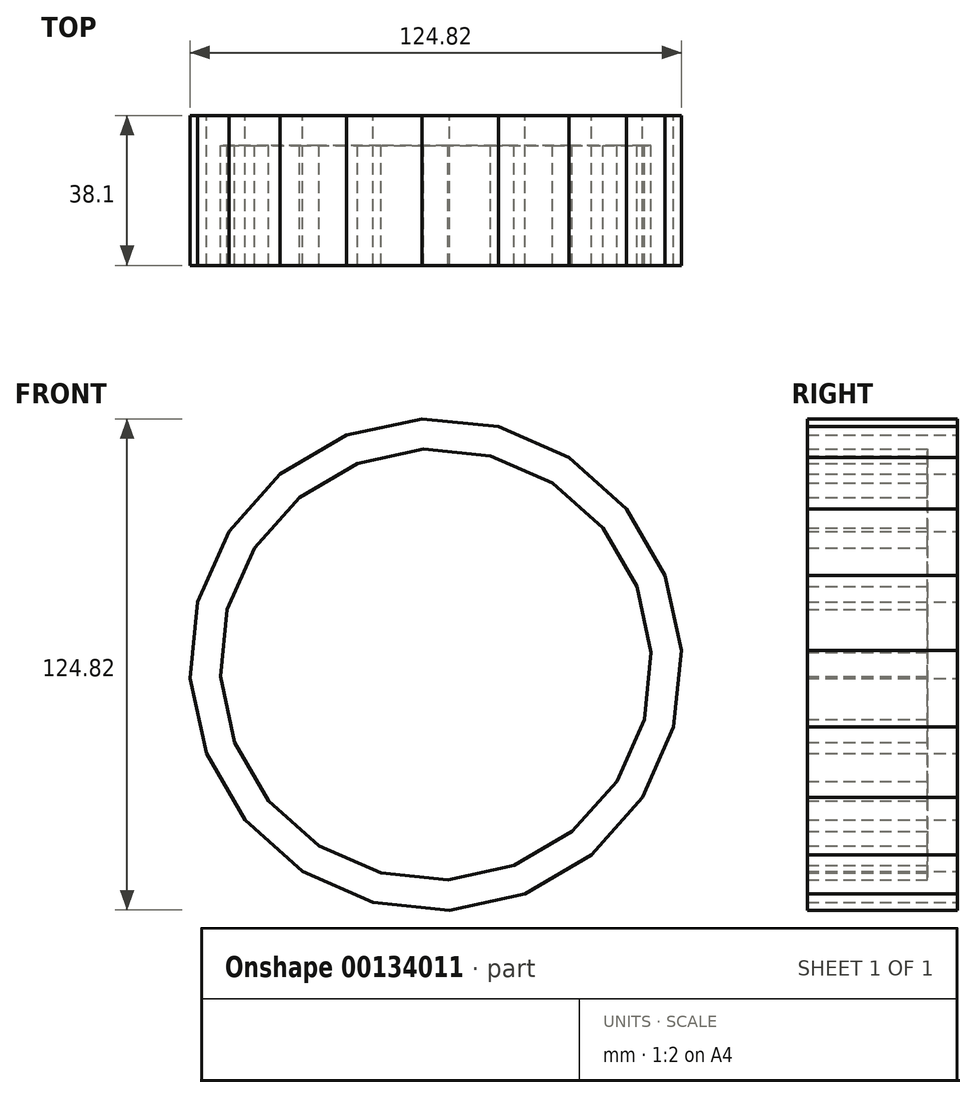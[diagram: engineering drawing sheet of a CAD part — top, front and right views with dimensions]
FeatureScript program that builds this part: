
annotation { "Feature Type Name" : "Feature", "Feature Type Description" : "" }
export const myFeature = defineFeature(function(context is Context, id is Id, definition is map)
    precondition{}
    {
        {
            var Q0;
            Q0=qCreatedBy(makeId("Front.planeOp"),FACE);
            var sketch = newSketch(context, id + "F0", { "sketchPlane" : qUnion([Q0])});
            skCircle(sketch, "E0.cCircle", {"center": v(0, 0) * mm, "radius": 61.74 * mm, "construction": true});
            skLineSegment(sketch, "E0.0", {"start": v(-48.41, -39.55) * mm, "end": v(-58.27, -22.65) * mm});
            skLineSegment(sketch, "E0.1", {"start": v(-58.27, -22.65) * mm, "end": v(-62.41, -3.54) * mm});
            skLineSegment(sketch, "E0.2", {"start": v(-62.41, -3.54) * mm, "end": v(-60.45, 15.92) * mm});
            skLineSegment(sketch, "E0.3", {"start": v(-60.45, 15.92) * mm, "end": v(-52.57, 33.82) * mm});
            skLineSegment(sketch, "E0.4", {"start": v(-52.57, 33.82) * mm, "end": v(-39.55, 48.41) * mm});
            skLineSegment(sketch, "E0.5", {"start": v(-39.55, 48.41) * mm, "end": v(-22.65, 58.27) * mm});
            skLineSegment(sketch, "E0.6", {"start": v(-22.65, 58.27) * mm, "end": v(-3.54, 62.41) * mm});
            skLineSegment(sketch, "E0.7", {"start": v(-3.54, 62.41) * mm, "end": v(15.92, 60.45) * mm});
            skLineSegment(sketch, "E0.8", {"start": v(15.92, 60.45) * mm, "end": v(33.82, 52.57) * mm});
            skLineSegment(sketch, "E0.9", {"start": v(33.82, 52.57) * mm, "end": v(48.41, 39.55) * mm});
            skLineSegment(sketch, "E0.10", {"start": v(48.41, 39.55) * mm, "end": v(58.27, 22.65) * mm});
            skLineSegment(sketch, "E0.11", {"start": v(58.27, 22.65) * mm, "end": v(62.41, 3.54) * mm});
            skLineSegment(sketch, "E0.12", {"start": v(62.41, 3.54) * mm, "end": v(60.45, -15.92) * mm});
            skLineSegment(sketch, "E0.13", {"start": v(60.45, -15.92) * mm, "end": v(52.57, -33.82) * mm});
            skLineSegment(sketch, "E0.14", {"start": v(52.57, -33.82) * mm, "end": v(39.55, -48.41) * mm});
            skLineSegment(sketch, "E0.15", {"start": v(39.55, -48.41) * mm, "end": v(22.65, -58.27) * mm});
            skLineSegment(sketch, "E0.16", {"start": v(22.65, -58.27) * mm, "end": v(3.54, -62.41) * mm});
            skLineSegment(sketch, "E0.17", {"start": v(3.54, -62.41) * mm, "end": v(-15.92, -60.45) * mm});
            skLineSegment(sketch, "E0.18", {"start": v(-15.92, -60.45) * mm, "end": v(-33.82, -52.57) * mm});
            skLineSegment(sketch, "E0.19", {"start": v(-33.82, -52.57) * mm, "end": v(-48.41, -39.55) * mm});
            skPoint(sketch, "E0.0.midPoint", {"position": v(-53.34, -31.1) * mm});
            skSolve(sketch);
        }
        {
            var Q0;
            Q0 = qSketchRegion(id + "F0", true);
            extrude(context, id + "F1", {"entities" : qUnion([Q0]), "endBound" : BoundingType.SYMMETRIC, "depth" : 38.1 * mm});
        }
        {
            var Q0;
            Q0=makeQuery(id+"F1.opExtrude","CAP_FACE",FACE,{"disambiguationData":[OSD([sQuery(id+"F0.wireOp",EDGE,"E0.0"),sQuery(id+"F0.wireOp",EDGE,"E0.1"),sQuery(id+"F0.wireOp",EDGE,"E0.2"),sQuery(id+"F0.wireOp",EDGE,"E0.3"),sQuery(id+"F0.wireOp",EDGE,"E0.4"),sQuery(id+"F0.wireOp",EDGE,"E0.5"),sQuery(id+"F0.wireOp",EDGE,"E0.6"),sQuery(id+"F0.wireOp",EDGE,"E0.7"),sQuery(id+"F0.wireOp",EDGE,"E0.8"),sQuery(id+"F0.wireOp",EDGE,"E0.9"),sQuery(id+"F0.wireOp",EDGE,"E0.10"),sQuery(id+"F0.wireOp",EDGE,"E0.11"),sQuery(id+"F0.wireOp",EDGE,"E0.12"),sQuery(id+"F0.wireOp",EDGE,"E0.13"),sQuery(id+"F0.wireOp",EDGE,"E0.14"),sQuery(id+"F0.wireOp",EDGE,"E0.15"),sQuery(id+"F0.wireOp",EDGE,"E0.16"),sQuery(id+"F0.wireOp",EDGE,"E0.17"),sQuery(id+"F0.wireOp",EDGE,"E0.18"),sQuery(id+"F0.wireOp",EDGE,"E0.19")])],"isStart":false});
            var Q1;
            Q1=makeQuery(id+"F1.opExtrude","SWEPT_BODY",BODY,{"disambiguationData":[OSD([sQuery(id+"F0.wireOp",EDGE,"E0.0"),sQuery(id+"F0.wireOp",EDGE,"E0.1"),sQuery(id+"F0.wireOp",EDGE,"E0.2"),sQuery(id+"F0.wireOp",EDGE,"E0.3"),sQuery(id+"F0.wireOp",EDGE,"E0.4"),sQuery(id+"F0.wireOp",EDGE,"E0.5"),sQuery(id+"F0.wireOp",EDGE,"E0.6"),sQuery(id+"F0.wireOp",EDGE,"E0.7"),sQuery(id+"F0.wireOp",EDGE,"E0.8"),sQuery(id+"F0.wireOp",EDGE,"E0.9"),sQuery(id+"F0.wireOp",EDGE,"E0.10"),sQuery(id+"F0.wireOp",EDGE,"E0.11"),sQuery(id+"F0.wireOp",EDGE,"E0.12"),sQuery(id+"F0.wireOp",EDGE,"E0.13"),sQuery(id+"F0.wireOp",EDGE,"E0.14"),sQuery(id+"F0.wireOp",EDGE,"E0.15"),sQuery(id+"F0.wireOp",EDGE,"E0.16"),sQuery(id+"F0.wireOp",EDGE,"E0.17"),sQuery(id+"F0.wireOp",EDGE,"E0.18"),sQuery(id+"F0.wireOp",EDGE,"E0.19")])]});
            shell(context, id + "F2", {"entities" : qUnion([Q0]), "parts" : qUnion([Q1]), "thickness" : 7.62 * mm});
        }
    });
